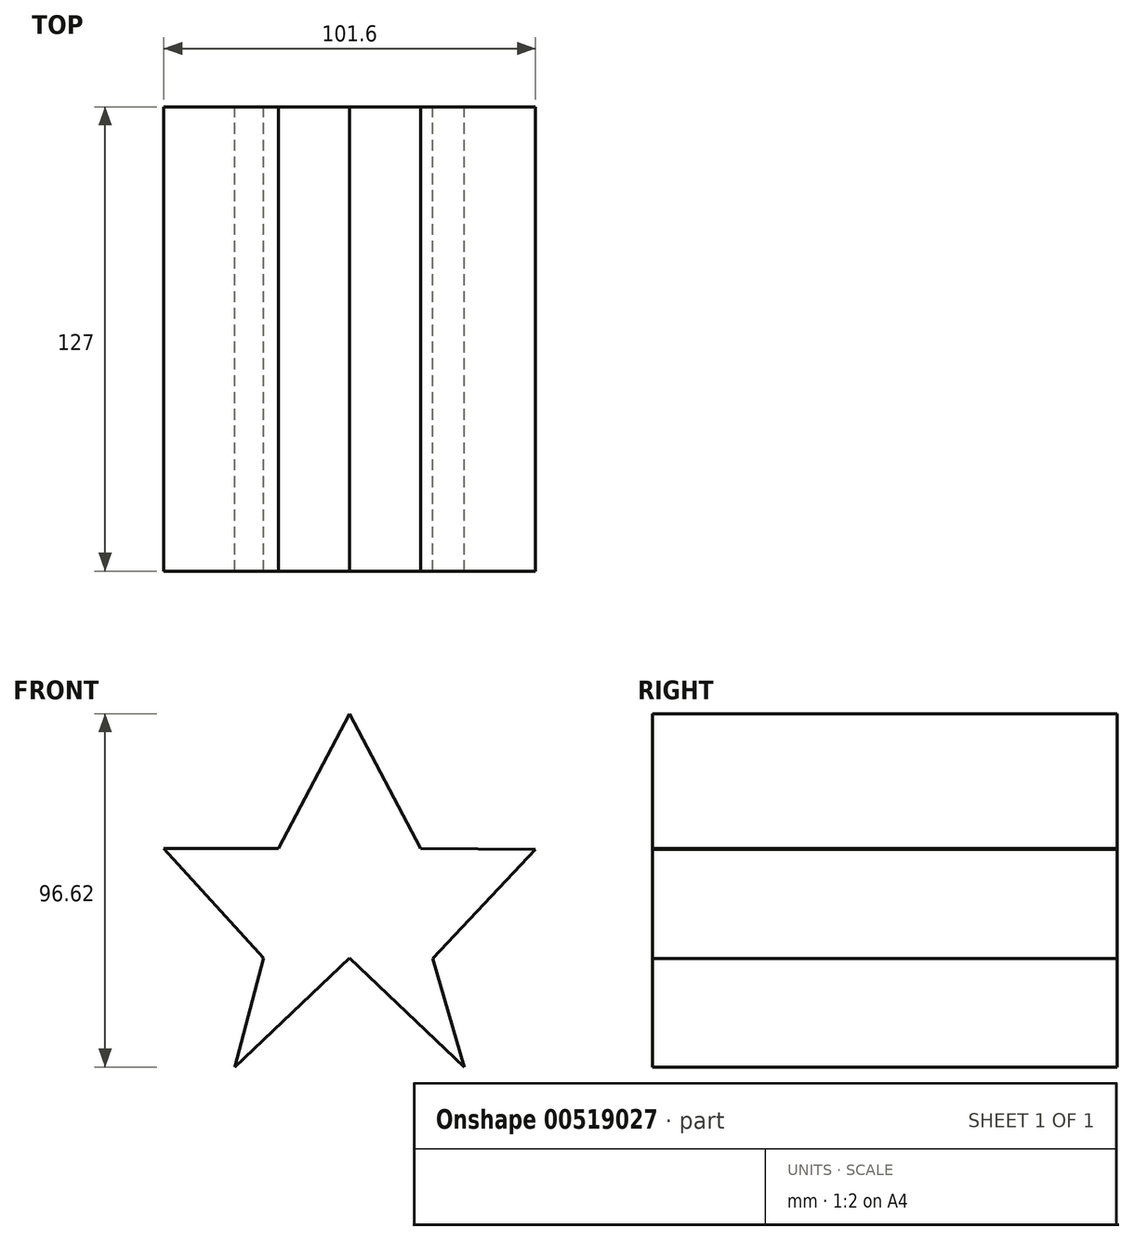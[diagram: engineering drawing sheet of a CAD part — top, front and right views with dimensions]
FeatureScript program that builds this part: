
annotation { "Feature Type Name" : "Feature", "Feature Type Description" : "" }
export const myFeature = defineFeature(function(context is Context, id is Id, definition is map)
    precondition{}
    {
        {
            var Q0;
            Q0=qCreatedBy(makeId("Front.planeOp"),FACE);
            var sketch = newSketch(context, id + "F0", { "sketchPlane" : qUnion([Q0])});
            skPoint(sketch, "E0.0.midPoint", {"position": v(25.4, 34.96) * mm});
            skLineSegment(sketch, "E1", {"start": v(0, 53.41) * mm, "end": v(-19.4, 16.5) * mm});
            skLineSegment(sketch, "E2", {"start": v(-19.4, 16.5) * mm, "end": v(-50.8, 16.5) * mm});
            skLineSegment(sketch, "E3", {"start": v(-50.8, 16.5) * mm, "end": v(-23.49, -13.35) * mm});
            skLineSegment(sketch, "E4", {"start": v(-23.49, -13.35) * mm, "end": v(-31.4, -43.21) * mm});
            skLineSegment(sketch, "E5", {"start": v(-31.4, -43.21) * mm, "end": v(0, -13.35) * mm});
            skLineSegment(sketch, "E6", {"start": v(0, -13.35) * mm, "end": v(31.4, -43.21) * mm});
            skLineSegment(sketch, "E7", {"start": v(22.7, -13.57) * mm, "end": v(50.8, 16.29) * mm});
            skLineSegment(sketch, "E8", {"start": v(19.4, 16.5) * mm, "end": v(0, 53.41) * mm});
            skLineSegment(sketch, "E9", {"start": v(22.7, -13.57) * mm, "end": v(31.4, -43.21) * mm});
            skLineSegment(sketch, "E10", {"start": v(19.4, 16.5) * mm, "end": v(50.8, 16.29) * mm});
            skSolve(sketch);
        }
        {
            var Q0;
            Q0 = qSketchRegion(id + "F0", true);
            extrude(context, id + "F1", {"entities" : qUnion([Q0]), "endBound" : BoundingType.SYMMETRIC, "depth" : 127 * mm, "offsetDistance" : 25.4 * mm});
        }
    });
